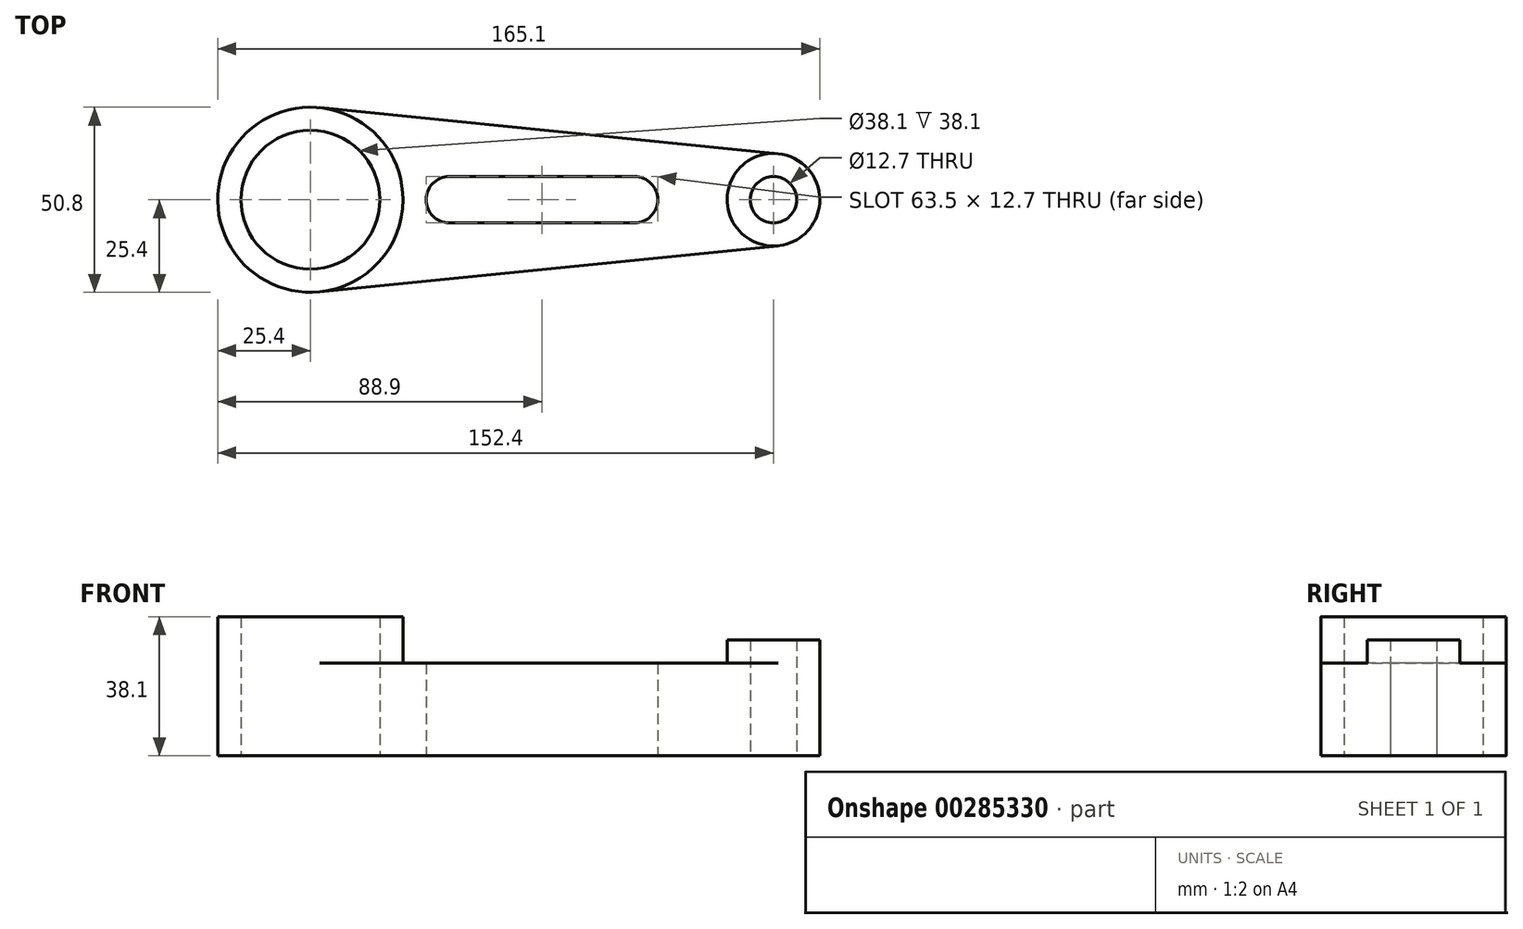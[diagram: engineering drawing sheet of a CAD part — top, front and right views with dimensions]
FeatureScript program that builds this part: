
annotation { "Feature Type Name" : "Feature", "Feature Type Description" : "" }
export const myFeature = defineFeature(function(context is Context, id is Id, definition is map)
    precondition{}
    {
        {
            var Q0;
            Q0=qCreatedBy(makeId("Top.planeOp"),FACE);
            var sketch = newSketch(context, id + "F0", { "sketchPlane" : qUnion([Q0])});
            skCircle(sketch, "E0", {"center": v(-38.1, 0) * mm, "radius": 19.05 * mm});
            skArc(sketch, "E1", {"start": v(0, 6.35) * mm, "mid": v(-6.35, 0) * mm, "end": v(0, -6.35) * mm});
            skArc(sketch, "E2", {"start": v(50.8, -6.35) * mm, "mid": v(57.15, 0) * mm, "end": v(50.8, 6.35) * mm});
            skCircle(sketch, "E3", {"center": v(88.9, 0) * mm, "radius": 6.35 * mm});
            skCircle(sketch, "E4", {"center": v(88.9, 0) * mm, "radius": 12.7 * mm});
            skCircle(sketch, "E5", {"center": v(-38.1, 0) * mm, "radius": 25.4 * mm});
            skLineSegment(sketch, "E6", {"start": v(-35.56, 25.27) * mm, "end": v(90.17, 12.64) * mm});
            skLineSegment(sketch, "E7", {"start": v(-35.56, -25.27) * mm, "end": v(90.17, -12.64) * mm});
            skLineSegment(sketch, "E8", {"start": v(0, 6.35) * mm, "end": v(50.8, 6.35) * mm});
            skLineSegment(sketch, "E9", {"start": v(0, -6.35) * mm, "end": v(50.8, -6.35) * mm});
            skSolve(sketch);
        }
        {
            var Q0;
            Q0=makeQuery(id+"F0.imprint","IMPRINT",FACE,{"disambiguationData":[TD([[makeQuery(id+"F0.imprint","IMPRINT",EDGE,{"derivedFrom":sQuery(id+"F0.wireOp",EDGE,"E0")}),-1.0]])]});
            extrude(context, id + "F1", {"entities" : qUnion([Q0]), "depth" : 38.1 * mm});
        }
        {
            var Q0;
            Q0=makeQuery(id+"F0.imprint","IMPRINT",FACE,{"disambiguationData":[TD([[makeQuery(id+"F0.imprint","IMPRINT",EDGE,{"derivedFrom":sQuery(id+"F0.wireOp",EDGE,"E1")}),-1.0]])]});
            extrude(context, id + "F2", {"entities" : qUnion([Q0]), "operationType" : NewBodyOperationType.ADD, "depth" : 25.4 * mm});
        }
        {
            var Q0;
            Q0=makeQuery(id+"F0.imprint","IMPRINT",FACE,{"disambiguationData":[TD([[makeQuery(id+"F0.imprint","IMPRINT",EDGE,{"derivedFrom":sQuery(id+"F0.wireOp",EDGE,"E3")}),-1.0]])]});
            extrude(context, id + "F3", {"entities" : qUnion([Q0]), "operationType" : NewBodyOperationType.ADD, "depth" : 31.75 * mm});
        }
    });
